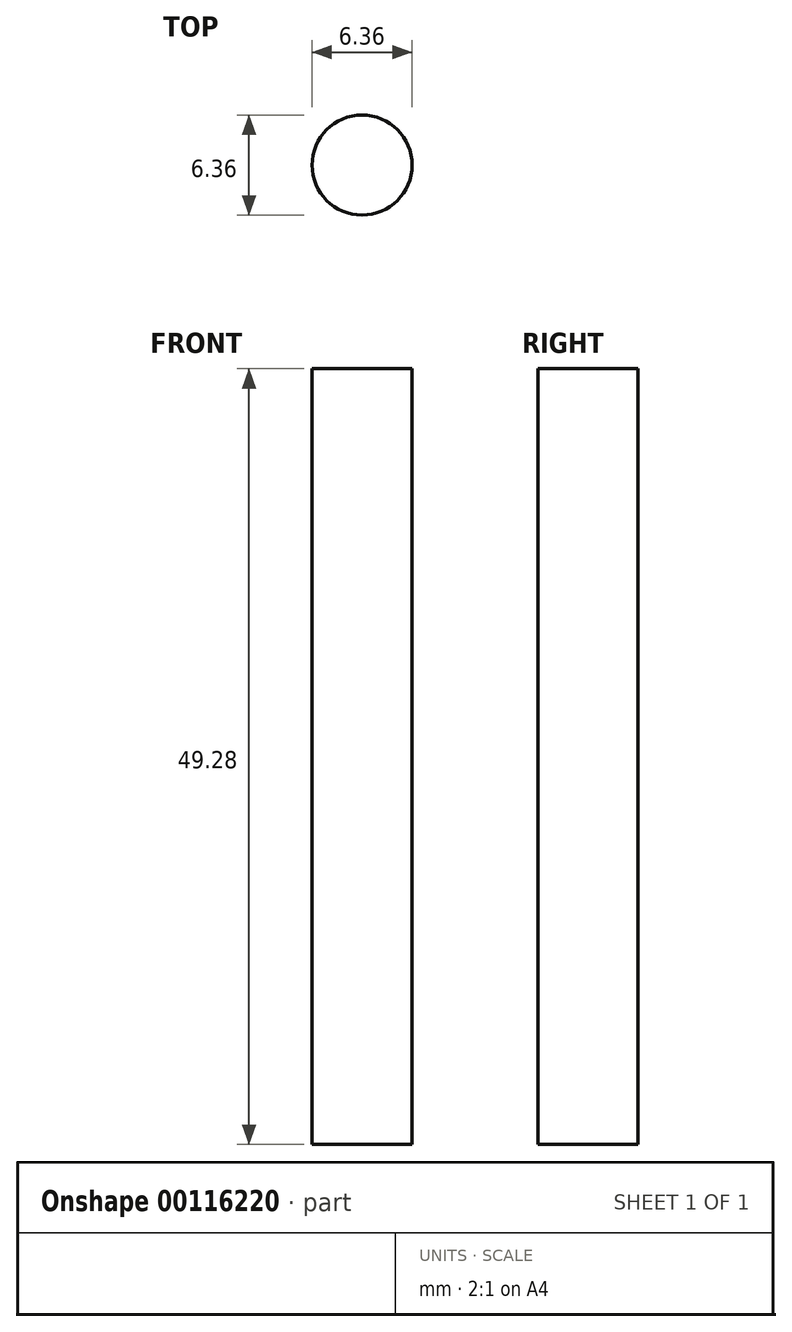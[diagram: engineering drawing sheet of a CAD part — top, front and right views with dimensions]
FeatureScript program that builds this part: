
annotation { "Feature Type Name" : "Feature", "Feature Type Description" : "" }
export const myFeature = defineFeature(function(context is Context, id is Id, definition is map)
    precondition{}
    {
        {
            var Q0;
            Q0=qCreatedBy(makeId("Top.planeOp"),FACE);
            var sketch = newSketch(context, id + "F0", { "sketchPlane" : qUnion([Q0])});
            skCircle(sketch, "E0", {"center": v(0, 0) * mm, "radius": 3.18 * mm});
            skSolve(sketch);
        }
        {
            var Q0;
            Q0 = qSketchRegion(id + "F0", true);
            extrude(context, id + "F1", {"entities" : qUnion([Q0]), "depth" : 49.28 * mm});
        }
    });
